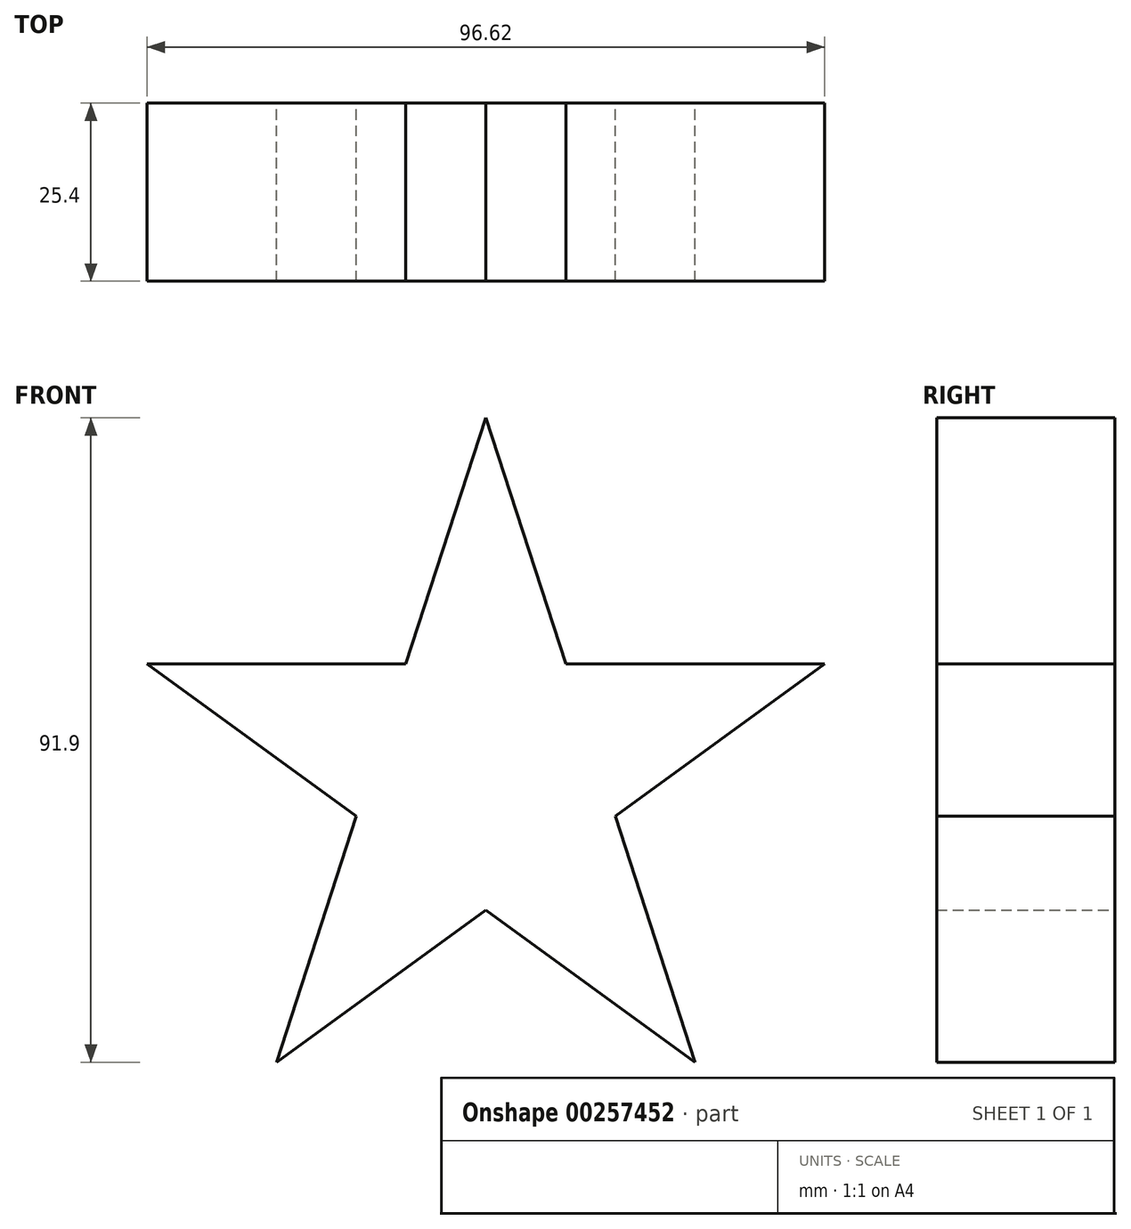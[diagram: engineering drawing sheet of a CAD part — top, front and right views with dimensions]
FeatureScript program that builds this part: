
annotation { "Feature Type Name" : "Feature", "Feature Type Description" : "" }
export const myFeature = defineFeature(function(context is Context, id is Id, definition is map)
    precondition{}
    {
        {
            var Q0;
            Q0=qCreatedBy(makeId("Front.planeOp"),FACE);
            var sketch = newSketch(context, id + "F0", { "sketchPlane" : qUnion([Q0])});
            skLineSegment(sketch, "E0", {"start": v(0, 50.8) * mm, "end": v(-11.4, 15.7) * mm});
            skLineSegment(sketch, "E1", {"start": v(0, 50.8) * mm, "end": v(11.4, 15.7) * mm});
            skLineSegment(sketch, "E2.1.0", {"start": v(-48.31, 15.7) * mm, "end": v(-18.45, -6) * mm});
            skLineSegment(sketch, "E2.1.1", {"start": v(-48.31, 15.7) * mm, "end": v(-11.4, 15.7) * mm});
            skLineSegment(sketch, "E2.2.0", {"start": v(-29.86, -41.1) * mm, "end": v(0, -19.4) * mm});
            skLineSegment(sketch, "E2.2.1", {"start": v(-29.86, -41.1) * mm, "end": v(-18.45, -6) * mm});
            skLineSegment(sketch, "E2.3.0", {"start": v(29.86, -41.1) * mm, "end": v(18.45, -6) * mm});
            skLineSegment(sketch, "E2.3.1", {"start": v(29.86, -41.1) * mm, "end": v(0, -19.4) * mm});
            skLineSegment(sketch, "E2.4.0", {"start": v(48.31, 15.7) * mm, "end": v(11.4, 15.7) * mm});
            skLineSegment(sketch, "E2.4.1", {"start": v(48.31, 15.7) * mm, "end": v(18.45, -6) * mm});
            skPoint(sketch, "E2.center", {"position": v(0, 0) * mm});
            skPoint(sketch, "E3.orphan", {"position": v(-15.28, 3.77) * mm});
            skPoint(sketch, "E4.orphan", {"position": v(-16.13, 1.17) * mm});
            skPoint(sketch, "E5.orphan", {"position": v(-8.31, -13.37) * mm});
            skPoint(sketch, "E6.orphan", {"position": v(-6.1, -14.98) * mm});
            skPoint(sketch, "E7.orphan", {"position": v(10.14, -12.03) * mm});
            skPoint(sketch, "E8.orphan", {"position": v(12.36, -10.42) * mm});
            skPoint(sketch, "E9.orphan", {"position": v(14.58, 5.93) * mm});
            skPoint(sketch, "E10.orphan", {"position": v(13.73, 8.53) * mm});
            skPoint(sketch, "E11.orphan", {"position": v(-1.13, 15.7) * mm});
            skPoint(sketch, "E12.orphan", {"position": v(-3.87, 15.7) * mm});
            skSolve(sketch);
        }
        {
            var Q0;
            Q0=makeQuery(id+"F0.imprint","IMPRINT",FACE,{"disambiguationData":[TD([[makeQuery(id+"F0.imprint","IMPRINT",EDGE,{"derivedFrom":sQuery(id+"F0.wireOp",EDGE,"E0")}),1.0]])]});
            extrude(context, id + "F1", {"entities" : qUnion([Q0]), "depth" : 25.4 * mm});
        }
    });
